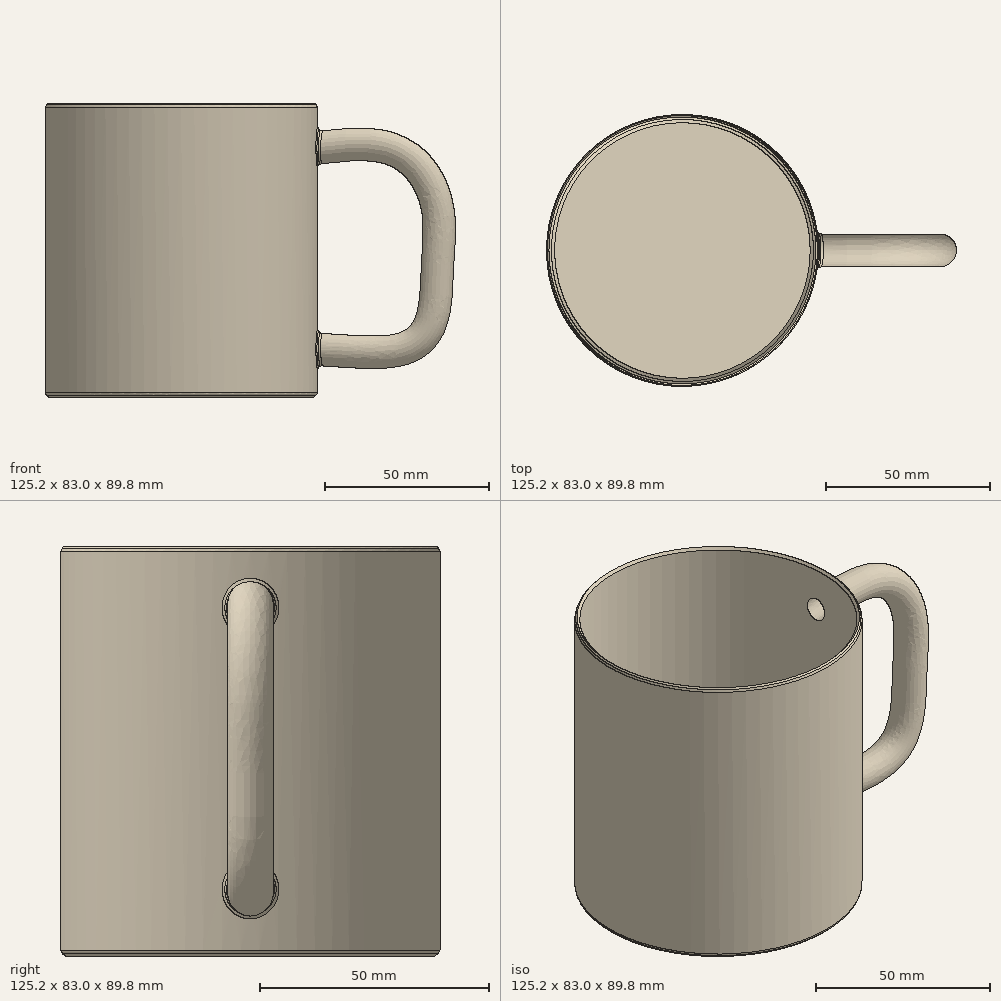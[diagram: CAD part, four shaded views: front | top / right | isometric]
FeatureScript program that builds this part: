
annotation { "Feature Type Name" : "Feature", "Feature Type Description" : "" }
export const myFeature = defineFeature(function(context is Context, id is Id, definition is map)
    precondition{}
    {
        {
            var Q0;
            Q0=qCreatedBy(makeId("Top.planeOp"),FACE);
            var sketch = newSketch(context, id + "F0", { "sketchPlane" : qUnion([Q0])});
            skCircle(sketch, "E0", {"center": v(0, 0) * mm, "radius": 41.5 * mm});
            skSolve(sketch);
        }
        {
            var Q0;
            Q0 = qSketchRegion(id + "F0", true);
            extrude(context, id + "F1", {"entities" : qUnion([Q0]), "depth" : 90 * mm, "offsetDistance" : 25 * mm});
        }
        {
            var Q0;
            Q0=qCreatedBy(makeId("Front.planeOp"),FACE);
            var sketch = newSketch(context, id + "F2", { "sketchPlane" : qUnion([Q0])});
            skFitSpline(sketch, "E1", {"points": [v(32.19, 75.3) * mm, v(63.43, 76.28) * mm, v(77.82, 60.22) * mm, v(78.38, 40.8) * mm, v(76.32, 22.91) * mm, v(66.29, 14.3) * mm, v(32.78, 14.47) * mm], "startDerivative": vector(114.83, 6.17) * mm, "endDerivative": vector(-149.31, -11.85) * mm});
            skSolve(sketch);
        }
        {
            var Q0;
            Q0=qCreatedBy(makeId("Right.planeOp"),FACE);
            cPlane(context, id + "F3", {"entities" : qUnion([Q0]), "cplaneType" : CPlaneType.OFFSET, "offset" : 36.7 * mm, "width" : 150 * mm, "height" : 150 * mm});
        }
        {
            var Q0;
            Q0=qCreatedBy(id+"F3.planeOp",FACE);
            var sketch = newSketch(context, id + "F4", { "sketchPlane" : qUnion([Q0])});
            skCircle(sketch, "E2", {"center": v(0, 75.55) * mm, "radius": 5 * mm});
            skSolve(sketch);
        }
        {
            var Q0;
            Q0 = qSketchRegion(id + "F4", true);
            var Q1;
            Q1 = qConstructionFilter(qBodyType(qCreatedBy(id + "F2" ,EDGE), BodyType.WIRE), ConstructionObject.NO);
            sweep(context, id + "F5", {"operationType" : NewBodyOperationType.ADD, "profiles" : qUnion([Q0]), "path" : qUnion([Q1])});
        }
        {
            var Q0;
            Q0=makeQuery(id+"F1.opExtrude","CAP_FACE",FACE,{"disambiguationData":[OSD([sQuery(id+"F0.wireOp",EDGE,"E0")])],"isStart":false});
            shell(context, id + "F6", {"entities" : qUnion([Q0]), "thickness" : 1.5 * mm});
        }
        {
            var Q0;
            {var subQ0=sQuery(id+"F0.wireOp",EDGE,"E0");Q0=makeQuery(id+"F6.opShell","OFFSET_EDGE",EDGE,{"disambiguationData":[OSD([subQ0]),TDD([makeQuery(id+"F1.opExtrude","CAP_EDGE",EDGE,{"disambiguationData":[OSD([subQ0])],"isStart":false})])]});}
            chamfer(context, id + "F7", {"entities" : qUnion([Q0]), "width" : 1 * mm, "tangentPropagation" : true});
        }
        {
            var Q0;
            Q0=makeQuery(id+"F1.opExtrude","CAP_EDGE",EDGE,{"disambiguationData":[OSD([sQuery(id+"F0.wireOp",EDGE,"E0")])],"isStart":false});
            chamfer(context, id + "F8", {"entities" : qUnion([Q0]), "width" : 1 * mm, "tangentPropagation" : true});
        }
        {
            var Q0;
            {var subQ0=sQuery(id+"F0.wireOp",EDGE,"E0");Q0=makeQuery(id+"F6.opShell","OFFSET_EDGE",EDGE,{"disambiguationData":[OSD([subQ0]),TDD([makeQuery(id+"F1.opExtrude","CAP_EDGE",EDGE,{"disambiguationData":[OSD([subQ0])],"isStart":true})])]});}
            var Q1;
            Q1=makeQuery(id+"F1.opExtrude","SWEPT_FACE",FACE,{"disambiguationData":[OSD([sQuery(id+"F0.wireOp",EDGE,"E0")])]});
            chamfer(context, id + "F9", {"entities" : qUnion([Q0, Q1]), "width" : 1 * mm, "tangentPropagation" : true});
        }
        {
            var Q0;
            {var subQ0=sQuery(id+"F0.wireOp",EDGE,"E0");Q0=makeQuery(id+"F9.opChamfer","BLEND_EDGE",EDGE,{"blendedFrom":[makeQuery(id+"F1.opExtrude","CAP_EDGE",EDGE,{"disambiguationData":[OSD([subQ0])],"isStart":true}),makeQuery(id+"F1.opExtrude","SWEPT_FACE",FACE,{"disambiguationData":[OSD([subQ0])]})],"blendedInto":[makeQuery(id+"F1.opExtrude","SWEPT_FACE",FACE,{"disambiguationData":[OSD([subQ0])]})]});}
            fillet(context, id + "F10", {"entities" : qUnion([Q0]), "radius" : 1 * mm, "tangentPropagation" : true, "allowEdgeOverflow" : false});
        }
        {
            var Q0;
            {var subQ0=makeQuery(id+"F1.opExtrude","SWEPT_FACE",FACE,{"disambiguationData":[OSD([sQuery(id+"F0.wireOp",EDGE,"E0")])]});Q0=makeQuery(id+"F9.opChamfer","BLEND_EDGE",EDGE,{"blendedFrom":[makeQuery(id+"F5.boolean.opBoolean","INTERSECT",EDGE,{"disambiguationData":[OD(1.0)],"derivedFrom":[subQ0,makeQuery(id+"F5.opSweep","SWEPT_FACE",FACE,{"disambiguationData":[OSD([sQuery(id+"F2.wireOp",EDGE,"E1"),sQuery(id+"F4.wireOp",EDGE,"E2")])]})]}),subQ0],"blendedInto":[subQ0]});}
            chamfer(context, id + "F11", {"entities" : qUnion([Q0]), "width" : 1 * mm, "tangentPropagation" : true});
        }
        {
            var Q0;
            {var subQ0=makeQuery(id+"F5.opSweep","SWEPT_FACE",FACE,{"disambiguationData":[OSD([sQuery(id+"F2.wireOp",EDGE,"E1"),sQuery(id+"F4.wireOp",EDGE,"E2")])]});Q0=makeQuery(id+"F9.opChamfer","BLEND_EDGE",EDGE,{"blendedFrom":[makeQuery(id+"F5.boolean.opBoolean","INTERSECT",EDGE,{"disambiguationData":[OD(1.0)],"derivedFrom":[makeQuery(id+"F1.opExtrude","SWEPT_FACE",FACE,{"disambiguationData":[OSD([sQuery(id+"F0.wireOp",EDGE,"E0")])]}),subQ0]}),subQ0],"blendedInto":[subQ0]});}
            chamfer(context, id + "F12", {"entities" : qUnion([Q0]), "width" : 1 * mm, "tangentPropagation" : true});
        }
        {
            var Q0;
            {var subQ0=makeQuery(id+"F5.opSweep","SWEPT_FACE",FACE,{"disambiguationData":[OSD([sQuery(id+"F2.wireOp",EDGE,"E1"),sQuery(id+"F4.wireOp",EDGE,"E2")])]});Q0=makeQuery(id+"F9.opChamfer","BLEND_EDGE",EDGE,{"blendedFrom":[makeQuery(id+"F5.boolean.opBoolean","INTERSECT",EDGE,{"disambiguationData":[OD(0.0)],"derivedFrom":[makeQuery(id+"F1.opExtrude","SWEPT_FACE",FACE,{"disambiguationData":[OSD([sQuery(id+"F0.wireOp",EDGE,"E0")])]}),subQ0]}),subQ0],"blendedInto":[subQ0]});}
            fillet(context, id + "F13", {"entities" : qUnion([Q0]), "radius" : 1 * mm, "tangentPropagation" : true, "allowEdgeOverflow" : false});
        }
        {
            var Q0;
            {var subQ0=makeQuery(id+"F1.opExtrude","SWEPT_FACE",FACE,{"disambiguationData":[OSD([sQuery(id+"F0.wireOp",EDGE,"E0")])]});Q0=makeQuery(id+"F9.opChamfer","BLEND_EDGE",EDGE,{"blendedFrom":[makeQuery(id+"F5.boolean.opBoolean","INTERSECT",EDGE,{"disambiguationData":[OD(0.0)],"derivedFrom":[subQ0,makeQuery(id+"F5.opSweep","SWEPT_FACE",FACE,{"disambiguationData":[OSD([sQuery(id+"F2.wireOp",EDGE,"E1"),sQuery(id+"F4.wireOp",EDGE,"E2")])]})]}),subQ0],"blendedInto":[subQ0]});}
            chamfer(context, id + "F14", {"entities" : qUnion([Q0]), "width" : 1 * mm, "tangentPropagation" : true});
        }
    });
